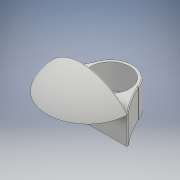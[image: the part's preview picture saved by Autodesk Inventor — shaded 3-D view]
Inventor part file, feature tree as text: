
AUTODESK INVENTOR PART (.ipt)
format: ipt  version: 2017 (Build 210142000, 142)  size: 233,472 bytes
history: native  units: mm
features: sketch x4, extrude x3, shell x2, revolve x1, fillet x1, projected_geometry x1
ambient origin geometry x8: Origin, YZ Plane, XZ Plane, XY Plane, X Axis, Y Axis, Z Axis, Center Point
bodies: Solid1 (feature_tree)
feature tree (12):
  extrude  "Extrusion1"  Depth=24.0mm
  extrude  "Extrusion2"  Depth=13.0mm
  shell  "Shell1"  Thickness=17.0mm
  revolve  "Revolution1"  [1 undecoded]
  extrude  "Extrusion3"  Depth=0.5mm
  shell  "Shell2"  Thickness=17.0mm
  fillet  "Fillet1"  Radius=24.0mm
  sketch  "Sketch1"  dims[d0=48.0mm d1=24.0mm]
  sketch  "Sketch2"  dims[d2=27.0mm d3=13.0mm d4=17.0mm d5=0.0mm]
  sketch  "Sketch3"  dims[d6=2.0mm d7=23.0mm]
  sketch  "Sketch4"  dims[d8=15.0mm d9=0.0mm d10=2.0mm d11=17.0mm d12=24.0mm d13=0.0mm d14=0.0mm d15=180.0deg d16=5.0mm d17=50.0mm d18=0.0mm d19=2.0mm d20=0.5mm]
  projected_geometry  "Projected Loop1"
note: 1 required parameter value undecoded (feature->parameter linkage not recoverable at this tier; creation-order binding heuristic only, values carry confidence <= 0.55)
